FCSTD DOCUMENT  (FreeCAD 1.0R39319 (Git))
Label: Ejercicio1-Caballo
License: All rights reserved
LicenseURL: https://en.wikipedia.org/wiki/All_rights_reserved
objects: Sketcher::SketchObject×1
note: 2 computed .brp shape members not serialized (recipe doc carries the construction recipe); baked Part::Feature solids carry a one-line shape summary decoded from their .brp

FEATURE [Sketcher::SketchObject] Sketch
  ArcFitTolerance = 1e-06
  FullyConstrained = true
  MakeInternals = false
  MapMode = 2
  sketch-geometry (24):
    g0: Circle [constr] CenterX=-29 CenterY=0 CenterZ=0 NormalX=0 NormalY=0 NormalZ=1 AngleXU=0 Radius=11
    g1: Circle [constr] CenterX=29 CenterY=0 CenterZ=0 NormalX=0 NormalY=0 NormalZ=1 AngleXU=0 Radius=11
    g2: LineSegment StartX=-37.5 StartY=-57 StartZ=0 EndX=-37.5 EndY=-71 EndZ=0
    g3: LineSegment StartX=-37.5 StartY=-71 StartZ=0 EndX=37.5 EndY=-71 EndZ=0
    g4: LineSegment StartX=37.5 StartY=-71 StartZ=0 EndX=37.5 EndY=-57 EndZ=0
    g5: LineSegment [constr] StartX=37.5 StartY=-57 StartZ=0 EndX=-37.5 EndY=-57 EndZ=0
    g6: ArcOfCircle CenterX=37.5 CenterY=-33.4687 CenterZ=0 NormalX=0 NormalY=0 NormalZ=1 AngleXU=0 Radius=23.5313 StartAngle=1.81951 EndAngle=4.71239
    g7: ArcOfCircle CenterX=-37.5 CenterY=-33.4687 CenterZ=0 NormalX=0 NormalY=0 NormalZ=1 AngleXU=0 Radius=23.5313 StartAngle=4.71239 EndAngle=7.60527
    g8: ArcOfCircle CenterX=-29 CenterY=0 CenterZ=0 NormalX=0 NormalY=0 NormalZ=1 AngleXU=0 Radius=11 StartAngle=2.92001 EndAngle=4.46368
    g9: ArcOfCircle CenterX=29 CenterY=0 CenterZ=0 NormalX=0 NormalY=0 NormalZ=1 AngleXU=0 Radius=11 StartAngle=4.9611 EndAngle=5.79404
    g10: ArcOfCircle CenterX=0.266545 CenterY=-6.59313 CenterZ=0 NormalX=0 NormalY=0 NormalZ=1 AngleXU=0 Radius=41 StartAngle=2.17168 EndAngle=2.92001
    g11: ArcOfCircle CenterX=-48.3556 CenterY=64.3427 CenterZ=0 NormalX=0 NormalY=0 NormalZ=1 AngleXU=0 Radius=45 StartAngle=5.31327 EndAngle=6.11375
    g12: Circle [constr] CenterX=-23 CenterY=59.7543 CenterZ=0 NormalX=0 NormalY=0 NormalZ=1 AngleXU=0 Radius=19
    g13: Circle [constr] CenterX=-45 CenterY=34 CenterZ=0 NormalX=0 NormalY=0 NormalZ=1 AngleXU=0 Radius=8
    g14: ArcOfCircle CenterX=-22.9717 CenterY=60 CenterZ=0 NormalX=0 NormalY=0 NormalZ=1 AngleXU=0 Radius=19.2473 StartAngle=4.59759 EndAngle=6.11375
    g15: ArcOfCircle CenterX=-26.4363 CenterY=29.9518 CenterZ=0 NormalX=0 NormalY=0 NormalZ=1 AngleXU=0 Radius=11 StartAngle=1.456 EndAngle=2.92688
    g16: ArcOfCircle CenterX=-45 CenterY=34 CenterZ=0 NormalX=0 NormalY=0 NormalZ=1 AngleXU=0 Radius=8 StartAngle=4.04952 EndAngle=6.06847
    g17: LineSegment StartX=-49.9231 StartY=27.6942 StartZ=0 EndX=-58 EndY=34 EndZ=0
    g18: LineSegment StartX=-58 StartY=34 StartZ=0 EndX=-30.6704 EndY=86 EndZ=0
    g19: LineSegment StartX=-30.6704 StartY=86 StartZ=0 EndX=-34 EndY=101 EndZ=0
    g20: LineSegment StartX=-34 StartY=101 StartZ=0 EndX=-17 EndY=86 EndZ=0
    g21: ArcOfCircle CenterX=2.59592 CenterY=57 CenterZ=0 NormalX=0 NormalY=0 NormalZ=1 AngleXU=0 Radius=35 StartAngle=1.13611 EndAngle=2.16504
    g22: ArcOfCircle CenterX=-4.98435 CenterY=40.674 CenterZ=0 NormalX=0 NormalY=0 NormalZ=1 AngleXU=0 Radius=53 StartAngle=0.196085 EndAngle=1.13611
    g23: ArcOfCircle CenterX=-35.8821 CenterY=34.5365 CenterZ=0 NormalX=0 NormalY=0 NormalZ=1 AngleXU=0 Radius=84.5014 StartAngle=5.79404 EndAngle=6.47927
  constraints (67):
    c: PointOnObject(g0,g-1)
    c: Symmetric(g0,g1,g-2)
    c: Equal(g0,g1)
    c: Radius(g1) = 11
    c: DistanceX(g0,g1) = 58
    c: Coincident(g2,g3)
    c: Coincident(g3,g4)
    c: Coincident(g4,g5)
    c: Coincident(g5,g2)
    c: Vertical(g2)
    c: Vertical(g4)
    c: Horizontal(g3)
    c: Horizontal(g5)
    c: Distance(g2,g4) = 75
    c: Distance(g3,g5) = 14
    c: Coincident(g6,g4)
    c: Coincident(g7,g2)
    c: Tangent(g6,g5)
    c: Tangent(g7,g5)
    c: Equal(g7,g6)
    c: Distance(g4,g-1) = 57
    c: Tangent(g6,g1) = 1.5708
    c: Tangent(g7,g0) = 1.5708
    c: Coincident(g8,g0)
    c: Coincident(g8,g7)
    c: Coincident(g9,g1)
    c: Coincident(g9,g6)
    c: Tangent(g10,g8) = -1.5708
    c: Tangent(g11,g10) = 1.5708
    c: Radius(g10) = 41
    c: Radius(g11) = 45
    c: DistanceY(g11,g12) = 3
    c: Distance(g12,g-2) = 23
    c: Diameter(g13) = 16
    c: Radius(g12) = 19
    c: Tangent(g14,g12) = -1.5708
    c: PointOnObject(g15,g13)
    c: Tangent(g16,g13) = -1.5708
    c: Tangent(g16,g17) = 1.5708
    c: Coincident(g17,g18)
    c: Tangent(g18,g12)
    c: Coincident(g18,g19)
    c: Coincident(g19,g20)
    c: Tangent(g15,g14) = 1.5708
    c: Tangent(g16,g15) = 1.5708
    c: Horizontal(g16,g17)
    c: DistanceY(g-1,g17) = 34
    c: DistanceY(g16,g14) = 26
    c: DistanceY(g14,g20) = 26
    c: DistanceY(g20,g20) = 15
    c: DistanceX(g20,g20) = 17
    c: Distance(g20,g-2) = 17
    c: Tangent(g14,g11) = -1.5708
    c: DistanceX(g16,g-1) = 45
    c: DistanceX(g17,g16) = 13
    c: Radius(g15) = 11
    c: Horizontal(g20,g18)
    c: Radius(g21) = 35
    c: Coincident(g21,g20)
    c: DistanceY(g16,g21) = 23
    c: DistanceY(g-1,g22) = 51
    c: DistanceX(g-1,g22) = 47
    c: Radius(g22) = 53
    c: Tangent(g23,g9) = -1.5708
    c: Tangent(g23,g22) = -1.5708
    c: Distance(g11,g-2) = 4
    c: Tangent(g22,g21) = -1.5708
